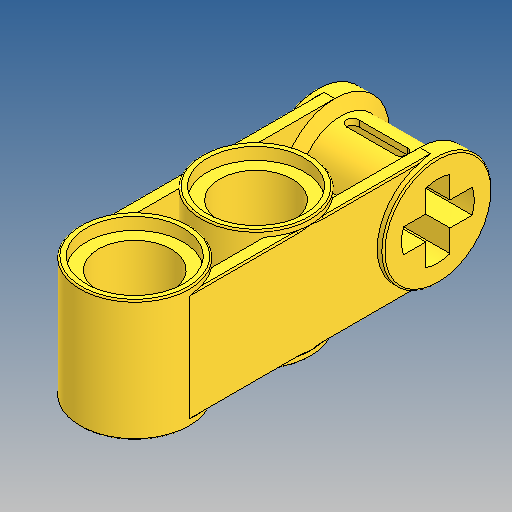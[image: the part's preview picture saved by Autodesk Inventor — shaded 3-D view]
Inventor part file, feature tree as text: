
AUTODESK INVENTOR PART (.ipt)
format: ipt  version: 2025 (Build 290162010, 162A)  size: 378,368 bytes
history: native  units: in
note: dims shown in document units (in); Inventor stores cm internally (conversion verified against a paired STEP export)
features: extrude x6, sketch x4, plane x1, mirror x1, revolve x1, fillet x1
ambient origin geometry x8: Origin, YZ Plane, XZ Plane, XY Plane, X Axis, Y Axis, Z Axis, Center Point
bodies: Solid1 (feature_tree)
feature tree (14):
  sketch  "Sketch2"  dims[d0=0.2835in d1=0.189in]
  extrude  "Extrusion1"  Depth=0.189in
  plane  "Work Plane1"
  extrude  "Extrusion2"  Depth=0.315in TaperAngle=0.0deg
  extrude  "Extrusion3"  Depth=0.2835in
  mirror  "Mirror1"
  revolve  "Revolution1"  [1 undecoded]
  extrude  "Extrusion4"  Depth=0.315in
  extrude  "Extrusion5"  Depth=0.0315in TaperAngle=0.0deg
  extrude  "Extrusion6"  Depth=0.2835in
  fillet  "Fillet1"  Radius=0.0472in
  sketch  "Sketch3"  dims[d2=0.315in d3=0.315in d4=0.0in]
  sketch  "Sketch4"  dims[d5=0.0in d6=0.2835in]
  sketch  "Sketch5"  dims[d7=0.0315in d8=0.315in d9=0.0in d10=0.252in d11=0.0315in d12=0.0in d13=0.2835in d14=0.0472in d15=0.315in d16=0.2205in d17=0.063in d18=0.0315in d19=0.1575in d20=90.0deg d21=0.063in d22=0.0in d23=0.063in d24=0.0in d25=0.189in d26=0.063in d27=0.063in d28=0.0in d29=0.0039in d30=0.315in]
note: 1 required parameter value undecoded (feature->parameter linkage not recoverable at this tier; creation-order binding heuristic only, values carry confidence <= 0.55)
